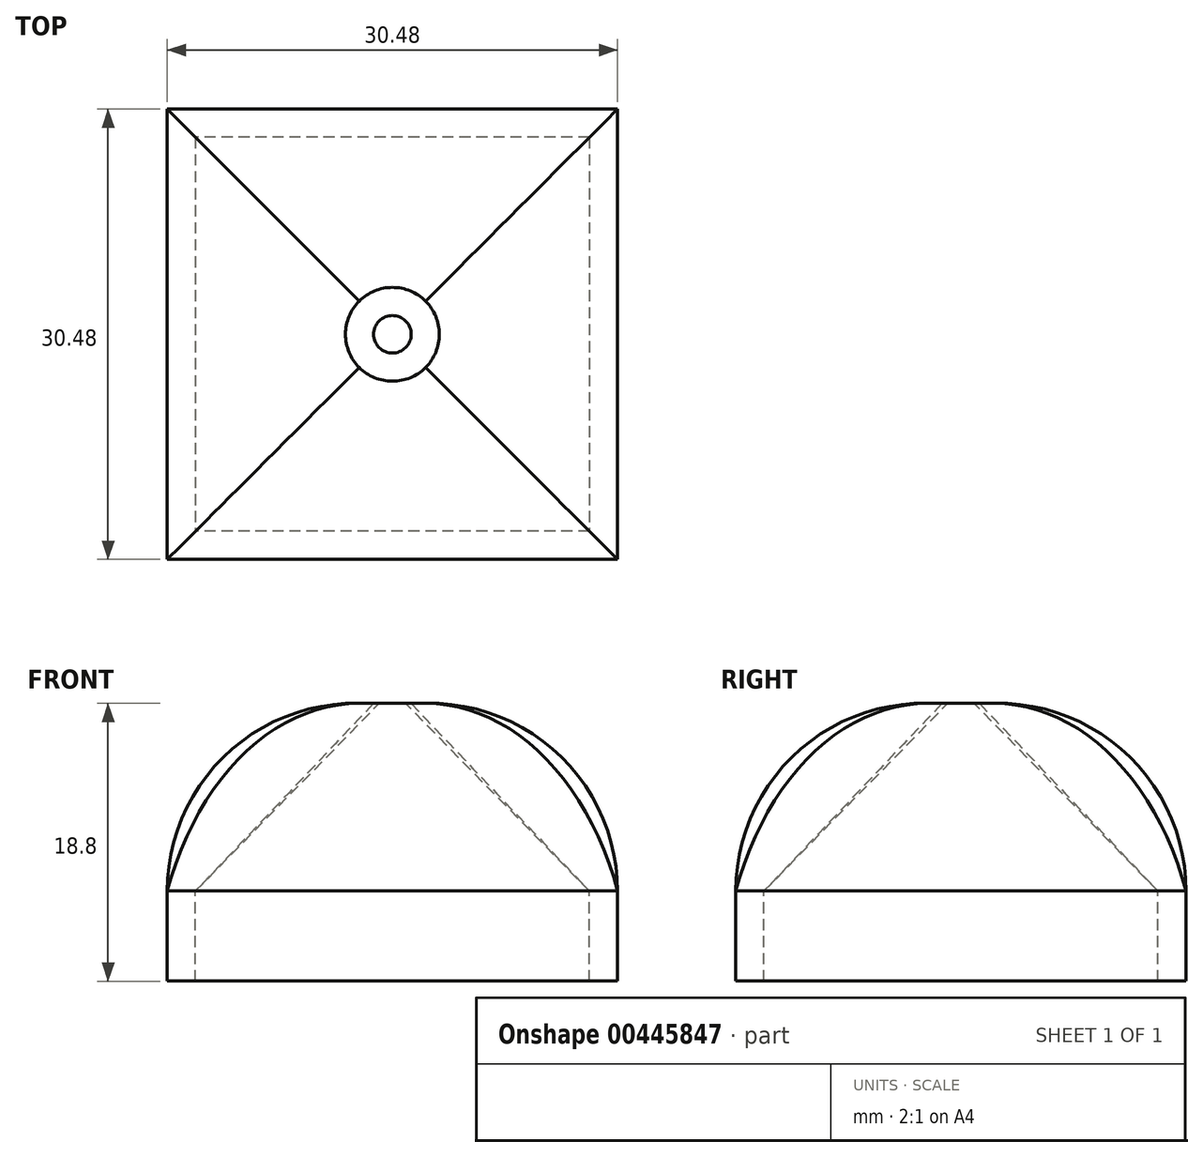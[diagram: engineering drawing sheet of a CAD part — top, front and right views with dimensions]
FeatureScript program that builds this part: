
annotation { "Feature Type Name" : "Feature", "Feature Type Description" : "" }
export const myFeature = defineFeature(function(context is Context, id is Id, definition is map)
    precondition{}
    {
        {
            var Q0;
            Q0=qCreatedBy(makeId("Top.planeOp"),FACE);
            var sketch = newSketch(context, id + "F0", { "sketchPlane" : qUnion([Q0])});
            skLineSegment(sketch, "E0.bottom", {"start": v(13.33, 13.34) * mm, "end": v(-13.34, 13.34) * mm});
            skLineSegment(sketch, "E0.top", {"start": v(13.34, -13.34) * mm, "end": v(-13.33, -13.34) * mm});
            skLineSegment(sketch, "E0.left", {"start": v(13.33, 13.34) * mm, "end": v(13.34, -13.34) * mm});
            skLineSegment(sketch, "E0.right", {"start": v(-13.34, 13.34) * mm, "end": v(-13.33, -13.34) * mm});
            skPoint(sketch, "E0.middle", {"position": v(0, 0) * mm});
            skLineSegment(sketch, "E1.0", {"start": v(15.24, -15.24) * mm, "end": v(-15.24, -15.24) * mm});
            skLineSegment(sketch, "E1.1", {"start": v(15.24, 15.24) * mm, "end": v(15.24, -15.24) * mm});
            skLineSegment(sketch, "E1.2", {"start": v(15.24, 15.24) * mm, "end": v(-15.24, 15.24) * mm});
            skLineSegment(sketch, "E1.3", {"start": v(-15.24, 15.24) * mm, "end": v(-15.24, -15.24) * mm});
            skSolve(sketch);
        }
        {
            var Q0;
            Q0=makeQuery(id+"F0.imprint","IMPRINT",FACE,{"disambiguationData":[TD([[makeQuery(id+"F0.imprint","IMPRINT",EDGE,{"derivedFrom":sQuery(id+"F0.wireOp",EDGE,"E0.bottom")}),-1.0]])]});
            extrude(context, id + "F1", {"entities" : qUnion([Q0]), "oppositeDirection" : true, "depth" : 2.3 * mm});
        }
        {
            var Q0;
            Q0=makeQuery(id+"F0.imprint","IMPRINT",FACE,{"disambiguationData":[TD([[makeQuery(id+"F0.imprint","IMPRINT",EDGE,{"derivedFrom":sQuery(id+"F0.wireOp",EDGE,"E0.bottom")}),-1.0]])]});
            extrude(context, id + "F2", {"entities" : qUnion([Q0]), "operationType" : NewBodyOperationType.ADD, "depth" : 3.8 * mm});
        }
        {
            var Q0;
            Q0=makeQuery(id+"F2.opExtrude","CAP_FACE",FACE,{"disambiguationData":[OSD([sQuery(id+"F0.wireOp",EDGE,"E0.bottom"),sQuery(id+"F0.wireOp",EDGE,"E0.top"),sQuery(id+"F0.wireOp",EDGE,"E0.left"),sQuery(id+"F0.wireOp",EDGE,"E0.right"),sQuery(id+"F0.wireOp",EDGE,"E1.0"),sQuery(id+"F0.wireOp",EDGE,"E1.1"),sQuery(id+"F0.wireOp",EDGE,"E1.2"),sQuery(id+"F0.wireOp",EDGE,"E1.3")])],"isStart":false});
            cPlane(context, id + "F3", {"entities" : qUnion([Q0]), "cplaneType" : CPlaneType.OFFSET, "offset" : 12.7 * mm, "width" : 152.4 * mm, "height" : 152.4 * mm});
        }
        {
            var Q0;
            Q0=qCreatedBy(id+"F3.planeOp",FACE);
            var sketch = newSketch(context, id + "F4", { "sketchPlane" : qUnion([Q0])});
            skCircle(sketch, "E2", {"center": v(0, 0) * mm, "radius": 1.27 * mm});
            skCircle(sketch, "E3.0", {"center": v(0, 0) * mm, "radius": 3.18 * mm});
            skLineSegment(sketch, "E4", {"start": v(-15.24, 15.24) * mm, "end": v(15.24, -15.24) * mm});
            skLineSegment(sketch, "E5", {"start": v(15.24, 15.24) * mm, "end": v(-15.24, -15.24) * mm});
            skSolve(sketch);
        }
        {
            var Q0;
            Q0=makeQuery(id+"F2.opExtrude","CAP_FACE",FACE,{"disambiguationData":[OSD([sQuery(id+"F0.wireOp",EDGE,"E0.bottom"),sQuery(id+"F0.wireOp",EDGE,"E0.top"),sQuery(id+"F0.wireOp",EDGE,"E0.left"),sQuery(id+"F0.wireOp",EDGE,"E0.right"),sQuery(id+"F0.wireOp",EDGE,"E1.0"),sQuery(id+"F0.wireOp",EDGE,"E1.1"),sQuery(id+"F0.wireOp",EDGE,"E1.2"),sQuery(id+"F0.wireOp",EDGE,"E1.3")])],"isStart":false});
            var sketch = newSketch(context, id + "F5", { "sketchPlane" : qUnion([Q0])});
            skLineSegment(sketch, "E6.0.0", {"start": v(15.24, 15.24) * mm, "end": v(-15.24, 15.24) * mm});
            skLineSegment(sketch, "E6.0.1", {"start": v(-15.24, 15.24) * mm, "end": v(-15.24, -15.24) * mm});
            skLineSegment(sketch, "E6.0.2", {"start": v(-15.24, -15.24) * mm, "end": v(15.24, -15.24) * mm});
            skLineSegment(sketch, "E6.0.3", {"start": v(15.24, -15.24) * mm, "end": v(15.24, 15.24) * mm});
            skLineSegment(sketch, "E7.0", {"start": v(13.34, -13.34) * mm, "end": v(-13.33, -13.34) * mm});
            skLineSegment(sketch, "E8.0", {"start": v(-13.34, 13.34) * mm, "end": v(-13.33, -13.34) * mm});
            skLineSegment(sketch, "E9.0", {"start": v(13.33, 13.34) * mm, "end": v(13.34, -13.34) * mm});
            skLineSegment(sketch, "E10.0", {"start": v(13.33, 13.34) * mm, "end": v(-13.34, 13.34) * mm});
            skLineSegment(sketch, "E11", {"start": v(-15.24, -15.24) * mm, "end": v(-13.33, -13.34) * mm});
            skLineSegment(sketch, "E12", {"start": v(-15.24, 15.24) * mm, "end": v(-13.34, 13.34) * mm});
            skLineSegment(sketch, "E13", {"start": v(15.24, -15.24) * mm, "end": v(13.34, -13.34) * mm});
            skLineSegment(sketch, "E14", {"start": v(15.24, 15.24) * mm, "end": v(13.33, 13.34) * mm});
            skSolve(sketch);
        }
        {
            var Q0;
            Q0=qCreatedBy(makeId("Right.planeOp"),FACE);
            var sketch = newSketch(context, id + "F6", { "sketchPlane" : qUnion([Q0])});
            skLineSegment(sketch, "E15.0.0", {"start": v(15.24, -2.29) * mm, "end": v(15.24, 3.81) * mm});
            skLineSegment(sketch, "E15.0.1", {"start": v(15.24, 3.81) * mm, "end": v(-15.24, 3.81) * mm});
            skLineSegment(sketch, "E15.0.2", {"start": v(-15.24, 3.81) * mm, "end": v(-15.24, -2.29) * mm});
            skLineSegment(sketch, "E15.0.3", {"start": v(-15.24, -2.29) * mm, "end": v(15.24, -2.29) * mm});
            skPoint(sketch, "E16.0", {"position": v(-3.18, 16.51) * mm});
            skArc(sketch, "E17", {"start": v(-3.18, 16.51) * mm, "mid": v(-11.74, 12.57) * mm, "end": v(-15.24, 3.81) * mm});
            skLineSegment(sketch, "E18.0", {"start": v(-3.18, 16.51) * mm, "end": v(3.18, 16.51) * mm});
            skArc(sketch, "E19", {"start": v(15.24, 3.81) * mm, "mid": v(11.74, 12.57) * mm, "end": v(3.17, 16.51) * mm});
            skSolve(sketch);
        }
        {
            var Q0;
            Q0=qCreatedBy(makeId("Front.planeOp"),FACE);
            var sketch = newSketch(context, id + "F7", { "sketchPlane" : qUnion([Q0])});
            skLineSegment(sketch, "E20.0.0", {"start": v(15.24, -2.29) * mm, "end": v(15.24, 3.81) * mm});
            skLineSegment(sketch, "E20.0.1", {"start": v(15.24, 3.81) * mm, "end": v(-15.24, 3.81) * mm});
            skLineSegment(sketch, "E20.0.2", {"start": v(-15.24, 3.81) * mm, "end": v(-15.24, -2.29) * mm});
            skLineSegment(sketch, "E20.0.3", {"start": v(-15.24, -2.29) * mm, "end": v(15.24, -2.29) * mm});
            skLineSegment(sketch, "E21.0", {"start": v(-3.18, 16.51) * mm, "end": v(3.18, 16.51) * mm});
            skArc(sketch, "E22", {"start": v(-3.18, 16.51) * mm, "mid": v(-11.74, 12.57) * mm, "end": v(-15.24, 3.81) * mm});
            skArc(sketch, "E23", {"start": v(15.24, 3.81) * mm, "mid": v(11.74, 12.57) * mm, "end": v(3.17, 16.51) * mm});
            skSolve(sketch);
        }
        {
            var Q0;
            Q0=sQuery(id+"F5.wireOp",VERTEX,"E12.start");
            var Q1;
            Q1=sQuery(id+"F5.wireOp",VERTEX,"E13.start");
            var Q2;
            Q2=makeQuery(id+"F1.opExtrude","CAP_VERTEX",VERTEX,{"disambiguationData":[OSD([sQuery(id+"F0.wireOp",EDGE,"E1.0"),sQuery(id+"F0.wireOp",EDGE,"E1.1")])],"isStart":false});
            cPlane(context, id + "F8", {"entities" : qUnion([Q0, Q1, Q2]), "cplaneType" : CPlaneType.THREE_POINT, "offset" : 25.4 * mm, "width" : 152.4 * mm, "height" : 152.4 * mm});
        }
        {
            var Q0;
            Q0=qCreatedBy(id+"F8.planeOp",FACE);
            var sketch = newSketch(context, id + "F9", { "sketchPlane" : qUnion([Q0])});
            skPoint(sketch, "E24.0", {"position": v(21.55, 3.81) * mm});
            skPoint(sketch, "E25.0", {"position": v(-3.18, 16.51) * mm});
            skPoint(sketch, "E26.0", {"position": v(-21.55, 3.81) * mm});
            skLineSegment(sketch, "E27.0.0", {"start": v(0, -2.29) * mm, "end": v(0, 3.81) * mm});
            skLineSegment(sketch, "E27.0.1", {"start": v(0, 3.81) * mm, "end": v(21.55, 3.81) * mm});
            skLineSegment(sketch, "E27.0.2", {"start": v(21.55, 3.81) * mm, "end": v(21.55, -2.29) * mm});
            skLineSegment(sketch, "E27.0.3", {"start": v(21.55, -2.29) * mm, "end": v(0, -2.29) * mm});
            skLineSegment(sketch, "E28.0.0", {"start": v(-21.55, -2.29) * mm, "end": v(-21.55, 3.81) * mm});
            skLineSegment(sketch, "E28.0.1", {"start": v(-21.55, 3.81) * mm, "end": v(0, 3.81) * mm});
            skLineSegment(sketch, "E28.0.2", {"start": v(0, 3.81) * mm, "end": v(0, -2.29) * mm});
            skLineSegment(sketch, "E28.0.3", {"start": v(0, -2.29) * mm, "end": v(-21.55, -2.29) * mm});
            skArc(sketch, "E29", {"start": v(21.55, 3.8) * mm, "mid": v(14.34, 13.03) * mm, "end": v(3.18, 16.5) * mm});
            skArc(sketch, "E30", {"start": v(-3.18, 16.51) * mm, "mid": v(-14.34, 13.03) * mm, "end": v(-21.55, 3.81) * mm});
            skLineSegment(sketch, "E31.0", {"start": v(-1.27, 16.51) * mm, "end": v(1.27, 16.51) * mm});
            skLineSegment(sketch, "E32.0", {"start": v(-3.18, 16.51) * mm, "end": v(3.18, 16.51) * mm});
            skSolve(sketch);
        }
        {
            var Q0;
            Q0=sQuery(id+"F5.wireOp",VERTEX,"E6.0.2.start");
            var Q1;
            Q1=sQuery(id+"F5.wireOp",VERTEX,"E6.0.3.end");
            var Q2;
            Q2=makeQuery(id+"F1.opExtrude","CAP_VERTEX",VERTEX,{"disambiguationData":[OSD([sQuery(id+"F0.wireOp",EDGE,"E1.1"),sQuery(id+"F0.wireOp",EDGE,"E1.2")])],"isStart":false});
            cPlane(context, id + "F10", {"entities" : qUnion([Q0, Q1, Q2]), "cplaneType" : CPlaneType.THREE_POINT, "offset" : 25.4 * mm, "width" : 152.4 * mm, "height" : 152.4 * mm});
        }
        {
            var Q0;
            Q0=qCreatedBy(id+"F10.planeOp",FACE);
            var sketch = newSketch(context, id + "F11", { "sketchPlane" : qUnion([Q0])});
            skLineSegment(sketch, "E33.0.0", {"start": v(0, -2.29) * mm, "end": v(0, 3.81) * mm});
            skLineSegment(sketch, "E33.0.1", {"start": v(0, 3.81) * mm, "end": v(-21.55, 3.81) * mm});
            skLineSegment(sketch, "E33.0.2", {"start": v(-21.55, 3.81) * mm, "end": v(-21.55, -2.29) * mm});
            skLineSegment(sketch, "E33.0.3", {"start": v(-21.55, -2.29) * mm, "end": v(0, -2.29) * mm});
            skLineSegment(sketch, "E34.0.0", {"start": v(21.55, -2.29) * mm, "end": v(21.55, 3.81) * mm});
            skLineSegment(sketch, "E34.0.1", {"start": v(21.55, 3.81) * mm, "end": v(0, 3.81) * mm});
            skLineSegment(sketch, "E34.0.2", {"start": v(0, 3.81) * mm, "end": v(0, -2.29) * mm});
            skLineSegment(sketch, "E34.0.3", {"start": v(0, -2.29) * mm, "end": v(21.55, -2.29) * mm});
            skLineSegment(sketch, "E35.0", {"start": v(-3.18, 16.51) * mm, "end": v(3.18, 16.51) * mm});
            skArc(sketch, "E36", {"start": v(21.55, 3.81) * mm, "mid": v(14.34, 13.03) * mm, "end": v(3.17, 16.5) * mm});
            skArc(sketch, "E37", {"start": v(-3.18, 16.51) * mm, "mid": v(-14.34, 13.03) * mm, "end": v(-21.55, 3.81) * mm});
            skSolve(sketch);
        }
        {
            var Q1;
            Q1=makeQuery(id+"F5.imprint","IMPRINT",FACE,{"disambiguationData":[TD([[makeQuery(id+"F5.imprint","IMPRINT",EDGE,{"derivedFrom":sQuery(id+"F5.wireOp",EDGE,"E6.0.3")}),-1.0]])]});
            var Q2;
            {var subQ0=sQuery(id+"F4.wireOp",EDGE,"E5");var subQ1=sQuery(id+"F4.wireOp",EDGE,"E2");var subQ2=makeQuery(id+"F4.imprint","INTERSECT",VERTEX,{"disambiguationData":[OD(0.0)],"derivedFrom":[subQ1,subQ0]});Q2=makeQuery(id+"F4.imprint","IMPRINT",FACE,{"disambiguationData":[TD([[makeQuery(id+"F4.imprint","IMPRINT",EDGE,{"disambiguationData":[TD([[subQ2,1.0]])],"derivedFrom":subQ1}),-1.0]])]});}
            var Q3;
            Q3=sQuery(id+"F9.wireOp",EDGE,"E29");
            var Q4;
            Q4=sQuery(id+"F7.wireOp",EDGE,"E23");
            var Q5;
            Q5=sQuery(id+"F11.wireOp",EDGE,"E36");
            loft(context, id + "F12", {"operationType" : NewBodyOperationType.ADD, "addGuides" : true, "sheetProfilesArray" : [{ "sheetProfileEntities" : qUnion([Q1]) }, { "sheetProfileEntities" : qUnion([Q2]) }], "guidesArray" : [{ "guideEntities" : qUnion([Q3]), "guideDerivativeType" : LoftGuideDerivativeType.DEFAULT, "guideDerivativeMagnitude" : 1 }, { "guideEntities" : qUnion([Q4]), "guideDerivativeType" : LoftGuideDerivativeType.DEFAULT, "guideDerivativeMagnitude" : 1 }, { "guideEntities" : qUnion([Q5]), "guideDerivativeType" : LoftGuideDerivativeType.DEFAULT, "guideDerivativeMagnitude" : 1 }]});
        }
        {
            var Q1;
            Q1=makeQuery(id+"F5.imprint","IMPRINT",FACE,{"disambiguationData":[TD([[makeQuery(id+"F5.imprint","IMPRINT",EDGE,{"derivedFrom":sQuery(id+"F5.wireOp",EDGE,"E6.0.1")}),1.0]])]});
            var Q2;
            {var subQ0=sQuery(id+"F4.wireOp",EDGE,"E4");var subQ1=sQuery(id+"F4.wireOp",EDGE,"E2");var subQ2=makeQuery(id+"F4.imprint","INTERSECT",VERTEX,{"disambiguationData":[OD(0.0)],"derivedFrom":[subQ1,subQ0]});Q2=makeQuery(id+"F4.imprint","IMPRINT",FACE,{"disambiguationData":[TD([[makeQuery(id+"F4.imprint","IMPRINT",EDGE,{"disambiguationData":[TD([[subQ2,-1.0]])],"derivedFrom":subQ1}),-1.0]])]});}
            var Q3;
            Q3=sQuery(id+"F11.wireOp",EDGE,"E37");
            var Q4;
            Q4=sQuery(id+"F7.wireOp",EDGE,"E22");
            var Q5;
            Q5=sQuery(id+"F9.wireOp",EDGE,"E30");
            loft(context, id + "F13", {"operationType" : NewBodyOperationType.ADD, "addGuides" : true, "sheetProfilesArray" : [{ "sheetProfileEntities" : qUnion([Q1]) }, { "sheetProfileEntities" : qUnion([Q2]) }], "guidesArray" : [{ "guideEntities" : qUnion([Q3]), "guideDerivativeType" : LoftGuideDerivativeType.DEFAULT, "guideDerivativeMagnitude" : 1 }, { "guideEntities" : qUnion([Q4]), "guideDerivativeType" : LoftGuideDerivativeType.DEFAULT, "guideDerivativeMagnitude" : 1 }, { "guideEntities" : qUnion([Q5]), "guideDerivativeType" : LoftGuideDerivativeType.DEFAULT, "guideDerivativeMagnitude" : 1 }]});
        }
        {
            var Q1;
            Q1=makeQuery(id+"F5.imprint","IMPRINT",FACE,{"disambiguationData":[TD([[makeQuery(id+"F5.imprint","IMPRINT",EDGE,{"derivedFrom":sQuery(id+"F5.wireOp",EDGE,"E6.0.2")}),-1.0]])]});
            var Q2;
            {var subQ0=sQuery(id+"F4.wireOp",EDGE,"E5");var subQ1=sQuery(id+"F4.wireOp",EDGE,"E2");var subQ2=makeQuery(id+"F4.imprint","INTERSECT",VERTEX,{"disambiguationData":[OD(1.0)],"derivedFrom":[subQ1,subQ0]});Q2=makeQuery(id+"F4.imprint","IMPRINT",FACE,{"disambiguationData":[TD([[makeQuery(id+"F4.imprint","IMPRINT",EDGE,{"disambiguationData":[TD([[subQ2,-1.0]])],"derivedFrom":subQ1}),-1.0]])]});}
            var Q3;
            Q3=sQuery(id+"F11.wireOp",EDGE,"E37");
            var Q4;
            Q4=sQuery(id+"F6.wireOp",EDGE,"E17");
            var Q5;
            Q5=sQuery(id+"F9.wireOp",EDGE,"E29");
            loft(context, id + "F14", {"operationType" : NewBodyOperationType.ADD, "addGuides" : true, "sheetProfilesArray" : [{ "sheetProfileEntities" : qUnion([Q1]) }, { "sheetProfileEntities" : qUnion([Q2]) }], "guidesArray" : [{ "guideEntities" : qUnion([Q3]), "guideDerivativeType" : LoftGuideDerivativeType.DEFAULT, "guideDerivativeMagnitude" : 1 }, { "guideEntities" : qUnion([Q4]), "guideDerivativeType" : LoftGuideDerivativeType.DEFAULT, "guideDerivativeMagnitude" : 1 }, { "guideEntities" : qUnion([Q5]), "guideDerivativeType" : LoftGuideDerivativeType.DEFAULT, "guideDerivativeMagnitude" : 1 }]});
        }
        {
            var Q1;
            Q1=makeQuery(id+"F5.imprint","IMPRINT",FACE,{"disambiguationData":[TD([[makeQuery(id+"F5.imprint","IMPRINT",EDGE,{"derivedFrom":sQuery(id+"F5.wireOp",EDGE,"E6.0.0")}),1.0]])]});
            var Q2;
            {var subQ0=sQuery(id+"F4.wireOp",EDGE,"E4");var subQ1=sQuery(id+"F4.wireOp",EDGE,"E2");var subQ2=makeQuery(id+"F4.imprint","INTERSECT",VERTEX,{"disambiguationData":[OD(0.0)],"derivedFrom":[subQ1,subQ0]});Q2=makeQuery(id+"F4.imprint","IMPRINT",FACE,{"disambiguationData":[TD([[makeQuery(id+"F4.imprint","IMPRINT",EDGE,{"disambiguationData":[TD([[subQ2,1.0]])],"derivedFrom":subQ1}),-1.0]])]});}
            var Q3;
            Q3=sQuery(id+"F6.wireOp",EDGE,"E19");
            var Q4;
            Q4=sQuery(id+"F11.wireOp",EDGE,"E36");
            var Q5;
            Q5=sQuery(id+"F9.wireOp",EDGE,"E30");
            loft(context, id + "F15", {"operationType" : NewBodyOperationType.ADD, "addGuides" : true, "sheetProfilesArray" : [{ "sheetProfileEntities" : qUnion([Q1]) }, { "sheetProfileEntities" : qUnion([Q2]) }], "guidesArray" : [{ "guideEntities" : qUnion([Q3]), "guideDerivativeType" : LoftGuideDerivativeType.DEFAULT, "guideDerivativeMagnitude" : 1 }, { "guideEntities" : qUnion([Q4]), "guideDerivativeType" : LoftGuideDerivativeType.DEFAULT, "guideDerivativeMagnitude" : 1 }, { "guideEntities" : qUnion([Q5]), "guideDerivativeType" : LoftGuideDerivativeType.DEFAULT, "guideDerivativeMagnitude" : 1 }]});
        }
    });
